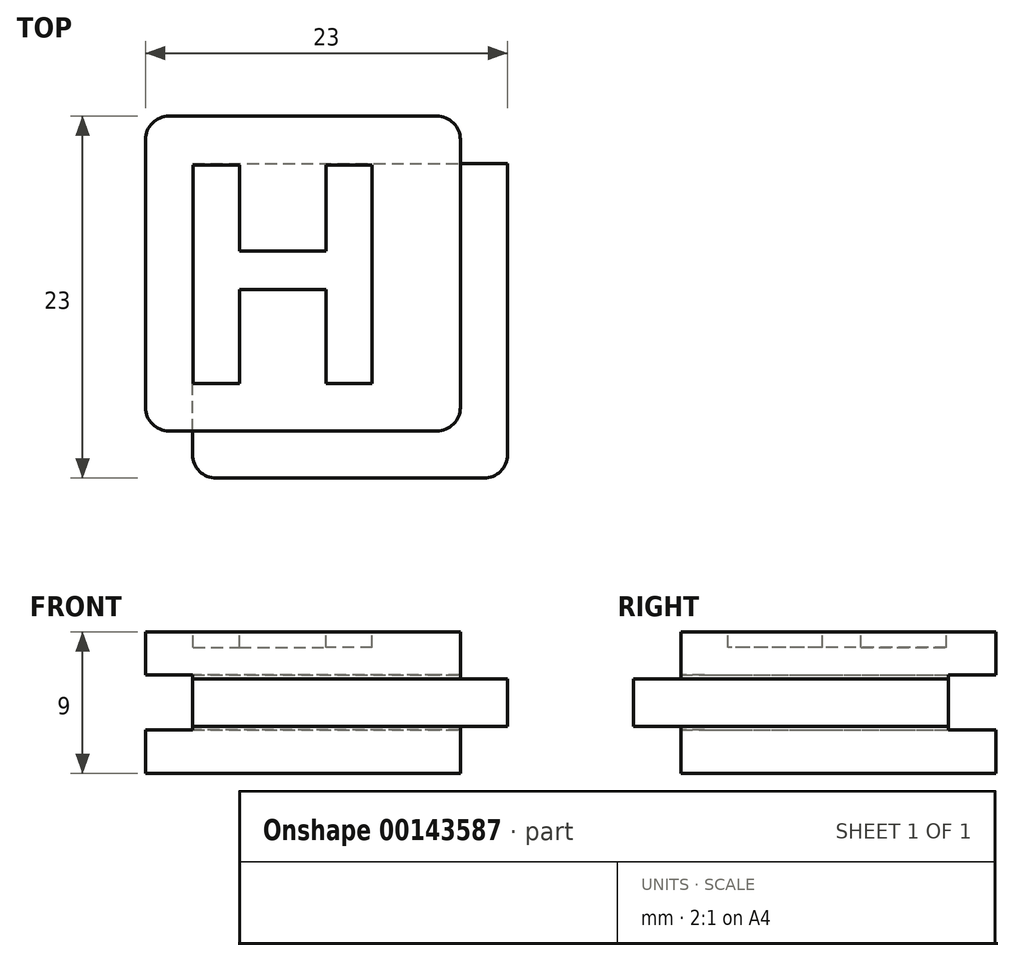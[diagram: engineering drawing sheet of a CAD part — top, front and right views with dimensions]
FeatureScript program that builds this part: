
annotation { "Feature Type Name" : "Feature", "Feature Type Description" : "" }
export const myFeature = defineFeature(function(context is Context, id is Id, definition is map)
    precondition{}
    {
        {
            var Q0;
            Q0=qCreatedBy(makeId("Front.planeOp"),FACE);
            var sketch = newSketch(context, id + "F0", { "sketchPlane" : qUnion([Q0])});
            skLineSegment(sketch, "E0.bottom", {"start": v(10, 4.5) * mm, "end": v(-10, 4.5) * mm});
            skLineSegment(sketch, "E0.top", {"start": v(10, -4.5) * mm, "end": v(-10, -4.5) * mm});
            skLineSegment(sketch, "E0.left", {"start": v(10, 4.5) * mm, "end": v(10, -4.5) * mm});
            skLineSegment(sketch, "E0.right", {"start": v(-10, 4.5) * mm, "end": v(-10, -4.5) * mm});
            skPoint(sketch, "E0.middle", {"position": v(0, 0) * mm});
            skLineSegment(sketch, "E1.bottom", {"start": v(13, 1.5) * mm, "end": v(7, 1.5) * mm});
            skLineSegment(sketch, "E1.top", {"start": v(13, -1.5) * mm, "end": v(7, -1.5) * mm});
            skLineSegment(sketch, "E1.left", {"start": v(13, 1.5) * mm, "end": v(13, -1.5) * mm});
            skLineSegment(sketch, "E1.right", {"start": v(7, 1.5) * mm, "end": v(7, -1.5) * mm});
            skPoint(sketch, "E1.middle", {"position": v(10, 0) * mm});
            skLineSegment(sketch, "E2.bottom", {"start": v(7, 1.5) * mm, "end": v(-7, 1.5) * mm});
            skLineSegment(sketch, "E2.top", {"start": v(7, -1.5) * mm, "end": v(-7, -1.5) * mm});
            skLineSegment(sketch, "E2.right", {"start": v(-7, 1.5) * mm, "end": v(-7, -1.5) * mm});
            skLineSegment(sketch, "E3.bottom", {"start": v(-7, -1.5) * mm, "end": v(-10, -1.5) * mm});
            skLineSegment(sketch, "E3.top", {"start": v(-7, 1.5) * mm, "end": v(-10, 1.5) * mm});
            skLineSegment(sketch, "E3.left", {"start": v(-7, -1.5) * mm, "end": v(-7, 1.5) * mm});
            skLineSegment(sketch, "E3.right", {"start": v(-10, -1.5) * mm, "end": v(-10, 1.5) * mm});
            skSolve(sketch);
        }
        {
            var Q0;
            {var subQ5=sQuery(id+"F0.wireOp",EDGE,"E0.bottom");Q0=makeQuery(id+"F0.imprint","IMPRINT",FACE,{"disambiguationData":[TD([[makeQuery(id+"F0.imprint","IMPRINT",EDGE,{"derivedFrom":subQ5}),1.0]])]});}
            var Q1;
            Q1=makeQuery(id+"F0.imprint","IMPRINT",FACE,{"disambiguationData":[TD([[makeQuery(id+"F0.imprint","IMPRINT",EDGE,{"derivedFrom":sQuery(id+"F0.wireOp",EDGE,"E2.bottom")}),1.0]])]});
            var Q2;
            {var subQ5=sQuery(id+"F0.wireOp",EDGE,"E1.left");Q2=makeQuery(id+"F0.imprint","IMPRINT",FACE,{"disambiguationData":[TD([[makeQuery(id+"F0.imprint","IMPRINT",EDGE,{"derivedFrom":subQ5}),-1.0]])]});}
            var Q3;
            {var subQ5=sQuery(id+"F0.wireOp",EDGE,"E1.right");Q3=makeQuery(id+"F0.imprint","IMPRINT",FACE,{"disambiguationData":[TD([[makeQuery(id+"F0.imprint","IMPRINT",EDGE,{"derivedFrom":subQ5}),1.0]])]});}
            var Q4;
            Q4=makeQuery(id+"F0.imprint","IMPRINT",FACE,{"disambiguationData":[TD([[makeQuery(id+"F0.imprint","IMPRINT",EDGE,{"derivedFrom":sQuery(id+"F0.wireOp",EDGE,"E3.bottom")}),-1.0]])]});
            var Q5;
            {var subQ5=sQuery(id+"F0.wireOp",EDGE,"E0.top");Q5=makeQuery(id+"F0.imprint","IMPRINT",FACE,{"disambiguationData":[TD([[makeQuery(id+"F0.imprint","IMPRINT",EDGE,{"derivedFrom":subQ5}),-1.0]])]});}
            extrude(context, id + "F1", {"entities" : qUnion([Q0, Q1, Q2, Q3, Q4, Q5]), "oppositeDirection" : true, "depth" : 20 * mm});
        }
        {
            var Q0;
            Q0=makeQuery(id+"F0.imprint","IMPRINT",FACE,{"disambiguationData":[TD([[makeQuery(id+"F0.imprint","IMPRINT",EDGE,{"derivedFrom":sQuery(id+"F0.wireOp",EDGE,"E3.bottom")}),-1.0]])]});
            var Q1;
            Q1=makeQuery(id+"F0.imprint","IMPRINT",FACE,{"disambiguationData":[TD([[makeQuery(id+"F0.imprint","IMPRINT",EDGE,{"derivedFrom":sQuery(id+"F0.wireOp",EDGE,"E2.bottom")}),1.0]])]});
            var Q2;
            {var subQ5=sQuery(id+"F0.wireOp",EDGE,"E1.right");Q2=makeQuery(id+"F0.imprint","IMPRINT",FACE,{"disambiguationData":[TD([[makeQuery(id+"F0.imprint","IMPRINT",EDGE,{"derivedFrom":subQ5}),1.0]])]});}
            var Q3;
            {var subQ5=sQuery(id+"F0.wireOp",EDGE,"E1.left");Q3=makeQuery(id+"F0.imprint","IMPRINT",FACE,{"disambiguationData":[TD([[makeQuery(id+"F0.imprint","IMPRINT",EDGE,{"derivedFrom":subQ5}),-1.0]])]});}
            extrude(context, id + "F2", {"entities" : qUnion([Q0, Q1, Q2, Q3]), "operationType" : NewBodyOperationType.ADD, "depth" : 3 * mm});
        }
        {
            var Q0;
            {var subQ0=sQuery(id+"F0.wireOp",EDGE,"E1.left");Q0=makeQuery(id+"F2.boolean.opBoolean","MERGE",FACE,{"derivedFrom":[makeQuery(id+"F1.opExtrude","SWEPT_FACE",FACE,{"disambiguationData":[OSD([subQ0])]}),makeQuery(id+"F2.opExtrude","SWEPT_FACE",FACE,{"disambiguationData":[OSD([subQ0])]})]});}
            var sketch = newSketch(context, id + "F3", { "sketchPlane" : qUnion([Q0])});
            skLineSegment(sketch, "E4.bottom", {"start": v(23, 1.75) * mm, "end": v(17, 1.75) * mm});
            skLineSegment(sketch, "E4.top", {"start": v(23, -1.75) * mm, "end": v(17, -1.75) * mm});
            skLineSegment(sketch, "E4.left", {"start": v(23, 1.75) * mm, "end": v(23, -1.75) * mm});
            skLineSegment(sketch, "E4.right", {"start": v(17, 1.75) * mm, "end": v(17, -1.75) * mm});
            skPoint(sketch, "E4.middle", {"position": v(20, 0) * mm});
            skSolve(sketch);
        }
        {
            var Q0;
            {var subQ1=sQuery(id+"F3.wireOp",EDGE,"E4.bottom");Q0=makeQuery(id+"F3.imprint","IMPRINT",FACE,{"disambiguationData":[TD([[makeQuery(id+"F3.imprint","IMPRINT",EDGE,{"derivedFrom":subQ1}),1.0]])]});}
            var Q1;
            {var subQ1=sQuery(id+"F0.wireOp",EDGE,"E1.left");var subQ8=makeQuery(id+"F1.opExtrude","CAP_EDGE",EDGE,{"disambiguationData":[OSD([subQ1])],"isStart":false});Q1=makeQuery(id+"F3.imprint","IMPRINT",FACE,{"disambiguationData":[TD([[makeQuery(id+"F3.imprint","IMPRINT",EDGE,{"derivedFrom":subQ8}),-1.0]])]});}
            extrude(context, id + "F4", {"entities" : qUnion([Q0, Q1]), "operationType" : NewBodyOperationType.REMOVE, "oppositeDirection" : true, "depth" : 100 * mm});
        }
        {
            var Q0;
            Q0=makeQuery(id+"F4.boolean.opBoolean","COPY",FACE,{"derivedFrom":makeQuery(id+"F4.opExtrude","SWEPT_FACE",FACE,{"disambiguationData":[OSD([sQuery(id+"F3.wireOp",EDGE,"E4.right")])]})});
            var sketch = newSketch(context, id + "F5", { "sketchPlane" : qUnion([Q0])});
            skLineSegment(sketch, "E5.bottom", {"start": v(13, 1.75) * mm, "end": v(7, 1.75) * mm});
            skLineSegment(sketch, "E5.top", {"start": v(13, -1.75) * mm, "end": v(7, -1.75) * mm});
            skLineSegment(sketch, "E5.left", {"start": v(13, 1.75) * mm, "end": v(13, -1.75) * mm});
            skLineSegment(sketch, "E5.right", {"start": v(7, 1.75) * mm, "end": v(7, -1.75) * mm});
            skPoint(sketch, "E5.middle", {"position": v(10, 0) * mm});
            skSolve(sketch);
        }
        {
            var Q0;
            {var subQ3=sQuery(id+"F5.wireOp",EDGE,"E5.left");Q0=makeQuery(id+"F5.imprint","IMPRINT",FACE,{"disambiguationData":[TD([[makeQuery(id+"F5.imprint","IMPRINT",EDGE,{"derivedFrom":subQ3}),-1.0]])]});}
            var Q1;
            {var subQ4=sQuery(id+"F5.wireOp",EDGE,"E5.right");Q1=makeQuery(id+"F5.imprint","IMPRINT",FACE,{"disambiguationData":[TD([[makeQuery(id+"F5.imprint","IMPRINT",EDGE,{"derivedFrom":subQ4}),1.0]])]});}
            extrude(context, id + "F6", {"entities" : qUnion([Q0, Q1]), "operationType" : NewBodyOperationType.REMOVE, "oppositeDirection" : true, "depth" : 100 * mm});
        }
        {
            var Q0;
            Q0=makeQuery(id+"F6.boolean.opBoolean","INTERSECT",EDGE,{"derivedFrom":[makeQuery(id+"F2.opExtrude","CAP_FACE",FACE,{"disambiguationData":[OSD([sQuery(id+"F0.wireOp",EDGE,"E1.bottom"),sQuery(id+"F0.wireOp",EDGE,"E1.top"),sQuery(id+"F0.wireOp",EDGE,"E1.left"),sQuery(id+"F0.wireOp",EDGE,"E2.bottom"),sQuery(id+"F0.wireOp",EDGE,"E2.top"),sQuery(id+"F0.wireOp",EDGE,"E3.bottom"),sQuery(id+"F0.wireOp",EDGE,"E3.top"),sQuery(id+"F0.wireOp",EDGE,"E3.right")])],"isStart":false}),makeQuery(id+"F6.opExtrude","SWEPT_FACE",FACE,{"disambiguationData":[OSD([sQuery(id+"F5.wireOp",EDGE,"E5.right")])]})]});
            var Q1;
            Q1=makeQuery(id+"F2.opExtrude","CAP_EDGE",EDGE,{"disambiguationData":[OSD([sQuery(id+"F0.wireOp",EDGE,"E1.left")])],"isStart":false});
            var Q2;
            {var subQ0=sQuery(id+"F0.wireOp",EDGE,"E0.left");Q2=makeQuery(id+"F1.opExtrude","CAP_EDGE",EDGE,{"disambiguationData":[OSD([subQ0]),TDD([makeQuery(id+"F0.imprint","IMPRINT",EDGE,{"disambiguationData":[TD([[makeQuery(id+"F0.imprint","INTERSECT",VERTEX,{"derivedFrom":[sQuery(id+"F0.wireOp",EDGE,"E0.bottom"),subQ0]}),-1.0]])],"derivedFrom":subQ0})])],"isStart":true});}
            var Q3;
            {var subQ0=sQuery(id+"F0.wireOp",EDGE,"E0.left");Q3=makeQuery(id+"F1.opExtrude","CAP_EDGE",EDGE,{"disambiguationData":[OSD([subQ0]),TDD([makeQuery(id+"F0.imprint","IMPRINT",EDGE,{"disambiguationData":[TD([[makeQuery(id+"F0.imprint","INTERSECT",VERTEX,{"derivedFrom":[sQuery(id+"F0.wireOp",EDGE,"E0.top"),subQ0]}),1.0]])],"derivedFrom":subQ0})])],"isStart":true});}
            var Q4;
            {var subQ0=sQuery(id+"F0.wireOp",EDGE,"E3.right");var subQ1=sQuery(id+"F0.wireOp",EDGE,"E0.right");var subQ3=sQuery(id+"F0.wireOp",EDGE,"E0.top");Q4=makeQuery(id+"F2.boolean.opBoolean","SPLIT",EDGE,{"disambiguationData":[TD([makeQuery(id+"F1.opExtrude","SWEPT_FACE",FACE,{"disambiguationData":[OSD([subQ3])]})])],"derivedFrom":makeQuery(id+"F1.opExtrude","CAP_EDGE",EDGE,{"disambiguationData":[OSD([subQ1,subQ0])],"isStart":true})});}
            var Q5;
            {var subQ1=sQuery(id+"F0.wireOp",EDGE,"E3.right");var subQ2=sQuery(id+"F0.wireOp",EDGE,"E0.right");var subQ3=sQuery(id+"F0.wireOp",EDGE,"E0.bottom");Q5=makeQuery(id+"F2.boolean.opBoolean","SPLIT",EDGE,{"disambiguationData":[TD([makeQuery(id+"F1.opExtrude","SWEPT_FACE",FACE,{"disambiguationData":[OSD([subQ3])]})])],"derivedFrom":makeQuery(id+"F1.opExtrude","CAP_EDGE",EDGE,{"disambiguationData":[OSD([subQ2,subQ1])],"isStart":true})});}
            var Q6;
            Q6=makeQuery(id+"F6.boolean.opBoolean","COPY",EDGE,{"derivedFrom":makeQuery(id+"F6.opExtrude","CAP_EDGE",EDGE,{"disambiguationData":[OSD([sQuery(id+"F5.wireOp",EDGE,"E5.right")])],"isStart":true})});
            var Q7;
            {var subQ0=sQuery(id+"F0.wireOp",EDGE,"E3.right");var subQ1=sQuery(id+"F0.wireOp",EDGE,"E0.right");var subQ2=sQuery(id+"F0.wireOp",EDGE,"E0.bottom");Q7=makeQuery(id+"F4.boolean.opBoolean","SPLIT",EDGE,{"disambiguationData":[TD([makeQuery(id+"F1.opExtrude","SWEPT_FACE",FACE,{"disambiguationData":[OSD([subQ2])]})])],"derivedFrom":makeQuery(id+"F1.opExtrude","CAP_EDGE",EDGE,{"disambiguationData":[OSD([subQ1,subQ0])],"isStart":false})});}
            var Q8;
            {var subQ0=sQuery(id+"F0.wireOp",EDGE,"E3.right");var subQ1=sQuery(id+"F0.wireOp",EDGE,"E0.right");var subQ2=sQuery(id+"F0.wireOp",EDGE,"E0.top");Q8=makeQuery(id+"F4.boolean.opBoolean","SPLIT",EDGE,{"disambiguationData":[TD([makeQuery(id+"F1.opExtrude","SWEPT_FACE",FACE,{"disambiguationData":[OSD([subQ2])]})])],"derivedFrom":makeQuery(id+"F1.opExtrude","CAP_EDGE",EDGE,{"disambiguationData":[OSD([subQ1,subQ0])],"isStart":false})});}
            var Q9;
            Q9=makeQuery(id+"F4.boolean.opBoolean","COPY",EDGE,{"derivedFrom":makeQuery(id+"F4.opExtrude","CAP_EDGE",EDGE,{"disambiguationData":[OSD([sQuery(id+"F3.wireOp",EDGE,"E4.right")])],"isStart":true})});
            var Q10;
            {var subQ0=sQuery(id+"F0.wireOp",EDGE,"E0.left");Q10=makeQuery(id+"F1.opExtrude","CAP_EDGE",EDGE,{"disambiguationData":[OSD([subQ0]),TDD([makeQuery(id+"F0.imprint","IMPRINT",EDGE,{"disambiguationData":[TD([[makeQuery(id+"F0.imprint","INTERSECT",VERTEX,{"derivedFrom":[sQuery(id+"F0.wireOp",EDGE,"E0.bottom"),subQ0]}),-1.0]])],"derivedFrom":subQ0})])],"isStart":false});}
            var Q11;
            {var subQ0=sQuery(id+"F0.wireOp",EDGE,"E0.left");Q11=makeQuery(id+"F1.opExtrude","CAP_EDGE",EDGE,{"disambiguationData":[OSD([subQ0]),TDD([makeQuery(id+"F0.imprint","IMPRINT",EDGE,{"disambiguationData":[TD([[makeQuery(id+"F0.imprint","INTERSECT",VERTEX,{"derivedFrom":[sQuery(id+"F0.wireOp",EDGE,"E0.top"),subQ0]}),1.0]])],"derivedFrom":subQ0})])],"isStart":false});}
            fillet(context, id + "F7", {"entities" : qUnion([Q0, Q1, Q2, Q3, Q4, Q5, Q6, Q7, Q8, Q9, Q10, Q11]), "radius" : 1.5 * mm, "tangentPropagation" : true, "allowEdgeOverflow" : false});
        }
        {
            var Q0;
            Q0=makeQuery(id+"F1.opExtrude","SWEPT_FACE",FACE,{"disambiguationData":[OSD([sQuery(id+"F0.wireOp",EDGE,"E0.bottom")])]});
            var sketch = newSketch(context, id + "F8", { "sketchPlane" : qUnion([Q0])});
            skText(sketch, "E6", { "text": "H", "fontName": "OpenSans-Bold.ttf"});
            skLineSegment(sketch, "E7.0", {"start": v(8, 3) * mm, "end": v(-11.07, 3) * mm});
            const initialGuessF8  = {"E6": [-0.00872, 0.003, 1, 0, 0.014]};
            skSetInitialGuess(sketch, initialGuessF8);
            skSolve(sketch);
        }
        {
            var Q0;
            {var subQ0=sQuery(id+"F8.wireOp",EDGE,"E6.sketch_text.stroke-1");Q0=makeQuery(id+"F8.imprint","IMPRINT",FACE,{"disambiguationData":[TD([[makeQuery(id+"F8.imprint","IMPRINT",EDGE,{"derivedFrom":subQ0}),-1.0]])]});}
            extrude(context, id + "F9", {"entities" : qUnion([Q0]), "operationType" : NewBodyOperationType.REMOVE, "oppositeDirection" : true, "depth" : 1 * mm});
        }
    });
